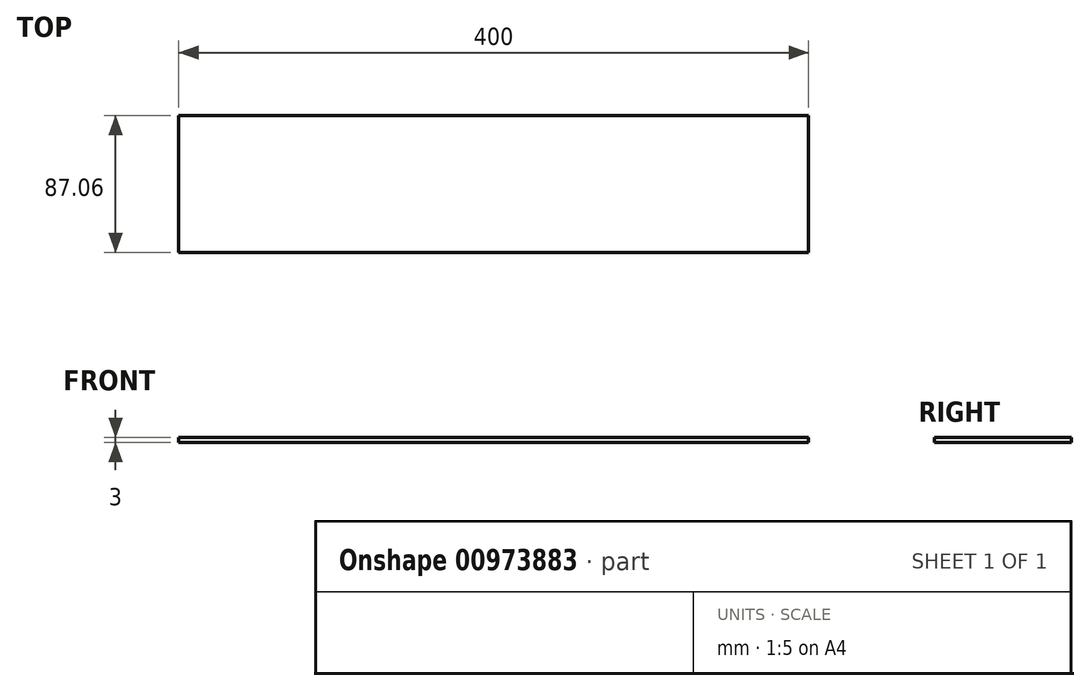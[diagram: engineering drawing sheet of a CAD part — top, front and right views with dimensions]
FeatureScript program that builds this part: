
annotation { "Feature Type Name" : "Feature", "Feature Type Description" : "" }
export const myFeature = defineFeature(function(context is Context, id is Id, definition is map)
    precondition{}
    {
        {
            var Q0;
            Q0=qCreatedBy(makeId("Top.planeOp"),FACE);
            var sketch = newSketch(context, id + "F0", { "sketchPlane" : qUnion([Q0])});
            skLineSegment(sketch, "E0.bottom", {"start": v(-200, 43.53) * mm, "end": v(200, 43.53) * mm});
            skLineSegment(sketch, "E0.top", {"start": v(-200, -43.53) * mm, "end": v(200, -43.53) * mm});
            skLineSegment(sketch, "E0.left", {"start": v(-200, 43.53) * mm, "end": v(-200, -43.53) * mm});
            skLineSegment(sketch, "E0.right", {"start": v(200, 43.53) * mm, "end": v(200, -43.53) * mm});
            skLineSegment(sketch, "E1", {"start": v(0, 0) * mm, "end": v(200, -43.53) * mm, "construction": true});
            skLineSegment(sketch, "E2", {"start": v(200, 43.53) * mm, "end": v(-200, -43.53) * mm, "construction": true});
            skSolve(sketch);
        }
        {
            var Q0;
            Q0 = qSketchRegion(id + "F0", true);
            extrude(context, id + "F1", {"entities" : qUnion([Q0]), "depth" : 3 * mm, "offsetDistance" : 25.4 * mm});
        }
    });
